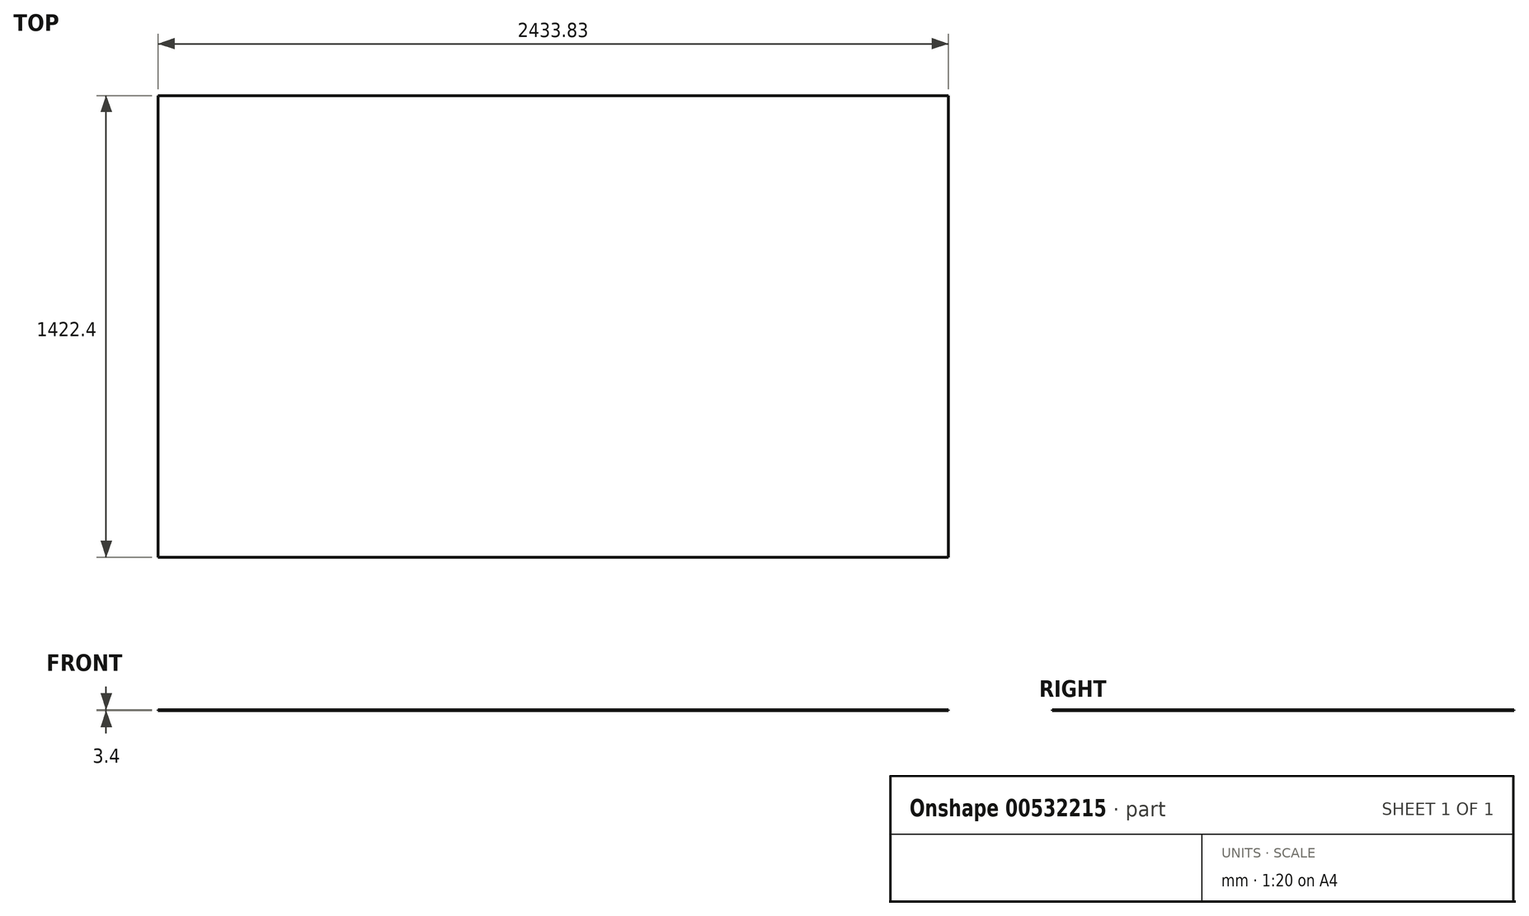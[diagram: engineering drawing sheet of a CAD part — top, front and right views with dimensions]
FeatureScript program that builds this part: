
annotation { "Feature Type Name" : "Feature", "Feature Type Description" : "" }
export const myFeature = defineFeature(function(context is Context, id is Id, definition is map)
    precondition{}
    {
        {
            var Q0;
            Q0=qCreatedBy(makeId("Top.planeOp"),FACE);
            var sketch = newSketch(context, id + "F0", { "sketchPlane" : qUnion([Q0])});
            skLineSegment(sketch, "E0.bottom", {"start": v(0, 0) * mm, "end": v(2433.83, 0) * mm});
            skLineSegment(sketch, "E0.top", {"start": v(0, 1422.4) * mm, "end": v(2433.83, 1422.4) * mm});
            skLineSegment(sketch, "E0.left", {"start": v(0, 0) * mm, "end": v(0, 1422.4) * mm});
            skLineSegment(sketch, "E0.right", {"start": v(2433.83, 0) * mm, "end": v(2433.83, 1422.4) * mm});
            skSolve(sketch);
        }
        {
            var Q0;
            Q0=makeQuery(id+"F0.imprint","IMPRINT",FACE,{"disambiguationData":[TD([[makeQuery(id+"F0.imprint","IMPRINT",EDGE,{"derivedFrom":sQuery(id+"F0.wireOp",EDGE,"E0.bottom")}),1.0]])]});
            extrude(context, id + "F1", {"entities" : qUnion([Q0]), "depth" : 3.4 * mm, "offsetDistance" : 25.4 * mm});
        }
    });
